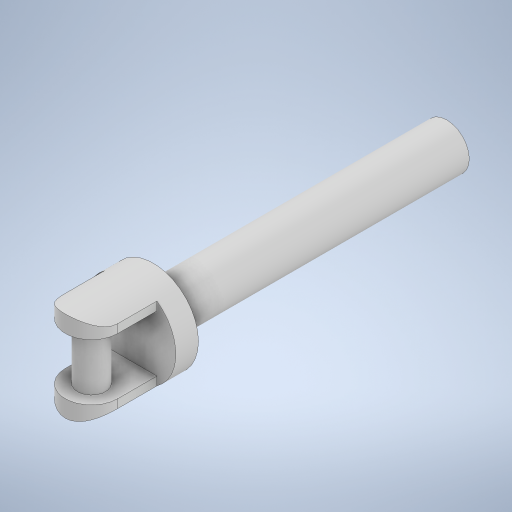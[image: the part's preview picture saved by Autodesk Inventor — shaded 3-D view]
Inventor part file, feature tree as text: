
AUTODESK INVENTOR PART (.ipt)
format: ipt  version: 2023 (Build 270158000, 158)  size: 291,840 bytes
history: native  units: in
note: dims shown in document units (in); Inventor stores cm internally (conversion verified against a paired STEP export)
features: sketch x5, extrude x4, revolve x1
ambient origin geometry x8: Origin, YZ Plane, XZ Plane, XY Plane, X Axis, Y Axis, Z Axis, Center Point
bodies: Solid1 (feature_tree)
feature tree (10):
  extrude  "Extrusion1"  Depth=2.0in TaperAngle=0.0deg
  revolve  "Revolution1"  [1 undecoded]
  extrude  "Extrusion2"  TaperAngle=90.0deg  [1 undecoded]
  extrude  "Extrusion3"  Depth=3.0in
  extrude  "Extrusion4"  Depth=10.0in TaperAngle=0.0deg
  sketch  "Sketch1"  dims[d0=2.0in d1=1.0in d2=0.0in]
  sketch  "Sketch2"  dims[d3=12.0in d4=0.0in d8=2.0in]
  sketch  "Sketch3"  dims[d9=4.0in d10=90.0deg]
  sketch  "Sketch4"  dims[d11=0.0in d12=3.0in]
  sketch  "Sketch5"  dims[d13=2.5in d14=10.0in d15=0.0in d16=0.4in d17=0.4in d19=10.0in d20=0.0in d21=1.25in d22=10.0in d23=0.0in d24=0.1in]
note: 2 required parameter values undecoded (feature->parameter linkage not recoverable at this tier; creation-order binding heuristic only, values carry confidence <= 0.55)